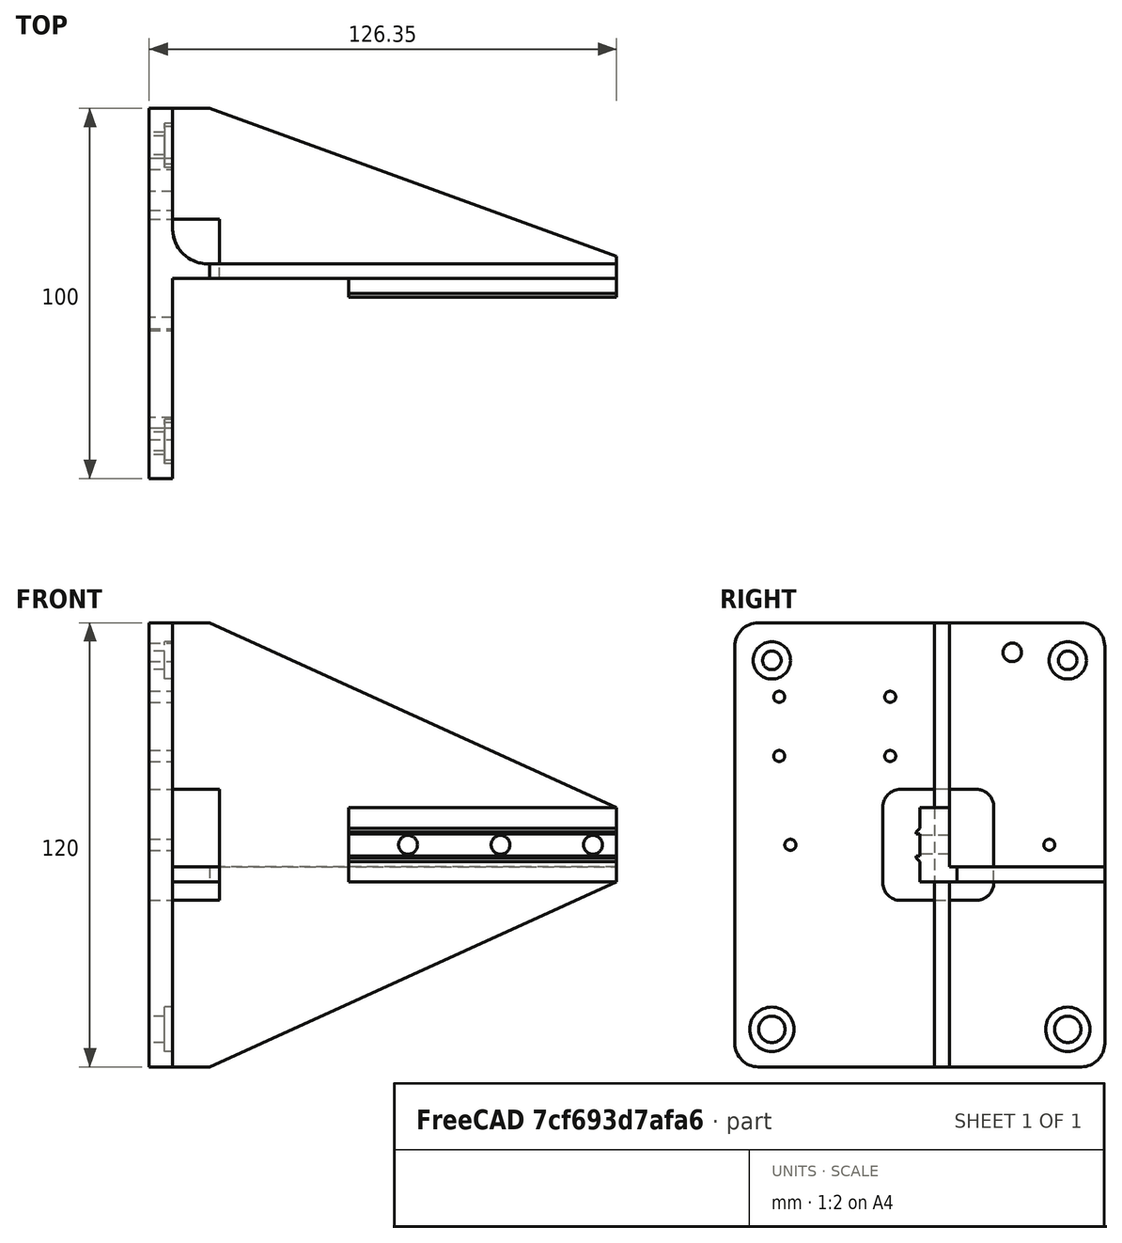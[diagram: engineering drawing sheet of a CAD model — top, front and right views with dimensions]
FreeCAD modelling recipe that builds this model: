
FCSTD DOCUMENT  (FreeCAD 0.19R23578 (Git))
Label: y_axis_carriage_block
License: All rights reserved
LicenseURL: http://en.wikipedia.org/wiki/All_rights_reserved
objects: TechDraw::DrawViewDimension×41, PartDesign::CoordinateSystem×15, Sketcher::SketchObject×10, PartDesign::Pocket×6, TechDraw::DrawProjGroupItem×3, TechDraw::DrawViewDimExtent×3, PartDesign::Pad×2, PartDesign::Fillet×2, PartDesign::Hole×2, TechDraw::DrawSVGTemplate×1, PartDesign::Body×1, TechDraw::DrawViewAnnotation×1, App::Part×1, TechDraw::DrawViewPart×1, TechDraw::DrawProjGroup×1, TechDraw::DrawViewDetail×1, TechDraw::DrawLeaderLine×1, TechDraw::DrawPage×1
note: 50 computed .brp shape members not serialized (recipe doc carries the construction recipe); baked Part::Feature solids carry a one-line shape summary decoded from their .brp

FEATURE [Sketcher::SketchObject] Sketch037
  MapMode = 5
  Support = -> [XY_Plane046]
  sketch-geometry (4):
    g0: LineSegment StartX=0 StartY=50 StartZ=0 EndX=6.35 EndY=50 EndZ=0
    g1: LineSegment StartX=6.35 StartY=50 StartZ=0 EndX=6.35 EndY=-50 EndZ=0
    g2: LineSegment StartX=6.35 StartY=-50 StartZ=0 EndX=0 EndY=-50 EndZ=0
    g3: LineSegment StartX=0 StartY=-50 StartZ=0 EndX=0 EndY=50 EndZ=0
  constraints (11):
    c: Coincident(g0,g1)
    c: Coincident(g1,g2)
    c: Coincident(g2,g3)
    c: Coincident(g3,g0)
    c: Horizontal(g0)
    c: Horizontal(g2)
    c: Vertical(g1)
    c: PointOnObject(g0,g-2)
    c: Symmetric(g2,g0,g-1)
    c: DistanceY(g2,g0) = 100
    c: DistanceX(g0,g0) = 6.35
FEATURE [PartDesign::Pad] Pad016
  AllowMultiFace = false
  Direction = (1,1,1)
  Length = 120
  Length2 = 100
  Midplane = true
  Profile = -> Sketch037
  Type = 0
FEATURE [Sketcher::SketchObject] Sketch038
  AttachmentOffset = pos=(0,0,6.35) rot=(0,0,1;0rad)
  MapMode = 5
  Placement = pos=(6.35,-1.4e-15,1.4e-15) rot=(0.57735,0.57735,0.57735;2.0944rad)
  Support = -> [YZ_Plane046]
  sketch-geometry (20):
    g0: LineSegment StartX=4 StartY=60 StartZ=0 EndX=4 EndY=10 EndZ=0
    g1: LineSegment StartX=4 StartY=10 StartZ=0 EndX=0 EndY=10 EndZ=0
    g2: LineSegment StartX=0 StartY=10 StartZ=0 EndX=0 EndY=4.5 EndZ=0
    g3: LineSegment StartX=0 StartY=4.5 StartZ=0 EndX=-1 EndY=3.5 EndZ=0
    g4: LineSegment StartX=-1 StartY=3.5 StartZ=0 EndX=-1 EndY=3 EndZ=0
    g5: LineSegment StartX=-1 StartY=3 StartZ=0 EndX=0 EndY=3 EndZ=0
    g6: LineSegment StartX=0 StartY=3 StartZ=0 EndX=0 EndY=-3 EndZ=0
    g7: LineSegment StartX=0 StartY=-3 StartZ=0 EndX=-1 EndY=-3 EndZ=0
    g8: LineSegment StartX=-1 StartY=-3 StartZ=0 EndX=-1 EndY=-3.5 EndZ=0
    g9: LineSegment StartX=-1 StartY=-3.5 StartZ=0 EndX=0 EndY=-4.5 EndZ=0
    g10: LineSegment StartX=0 StartY=-4.5 StartZ=0 EndX=0 EndY=-10 EndZ=0
    g11: LineSegment StartX=0 StartY=-10 StartZ=0 EndX=4 EndY=-10 EndZ=0
    g12: LineSegment StartX=4 StartY=-10 StartZ=0 EndX=4 EndY=-60 EndZ=0
    g13: LineSegment StartX=4 StartY=-60 StartZ=0 EndX=8 EndY=-60 EndZ=0
    g14: LineSegment StartX=8 StartY=-60 StartZ=0 EndX=8 EndY=-10 EndZ=0
    g15: LineSegment StartX=8 StartY=-10 StartZ=0 EndX=50 EndY=-10 EndZ=0
    g16: LineSegment StartX=50 StartY=-10 StartZ=0 EndX=50 EndY=-6 EndZ=0
    g17: LineSegment StartX=50 StartY=-6 StartZ=0 EndX=8 EndY=-6 EndZ=0
    g18: LineSegment StartX=8 StartY=-6 StartZ=0 EndX=8 EndY=60 EndZ=0
    g19: LineSegment StartX=8 StartY=60 StartZ=0 EndX=4 EndY=60 EndZ=0
  constraints (56):
    c: Vertical(g0)
    c: Coincident(g0,g1)
    c: Horizontal(g1)
    c: Coincident(g1,g2)
    c: Vertical(g2)
    c: Coincident(g2,g3)
    c: Coincident(g3,g4)
    c: Coincident(g4,g5)
    c: Horizontal(g5)
    c: Coincident(g5,g6)
    c: Coincident(g6,g7)
    c: Coincident(g7,g8)
    c: Coincident(g8,g9)
    c: Coincident(g9,g10)
    c: Vertical(g10)
    c: Coincident(g10,g11)
    c: Coincident(g11,g12)
    c: Vertical(g12)
    c: Coincident(g12,g13)
    c: Horizontal(g13)
    c: Coincident(g13,g14)
    c: Vertical(g14)
    c: Coincident(g14,g15)
    c: Horizontal(g15)
    c: Coincident(g15,g16)
    c: Coincident(g16,g17)
    c: Horizontal(g17)
    c: Coincident(g17,g18)
    c: Vertical(g18)
    c: Coincident(g18,g19)
    c: Coincident(g19,g0)
    c: Vertical(g4)
    c: Vertical(g6)
    c: Vertical(g16)
    c: Horizontal(g19)
    c: Horizontal(g7)
    c: Horizontal(g11)
    c: Vertical(g17,g14)
    c: Angle(g5,g3) = 0.785398
    c: Angle(g9,g7) = 0.785398
    c: DistanceY(g8,g8) = 0.5
    c: DistanceY(g6,g6) = 6
    c: Symmetric(g10,g1,g-1)
    c: Vertical(g9,g6)
    c: Symmetric(g7,g4,g-1)
    c: PointOnObject(g-1,g6)
    c: Symmetric(g3,g8,g-1)
    c: DistanceY(g-1,g2) = 4.5
    c: DistanceX(g1,g1) = 4
    c: Symmetric(g12,g0,g-1)
    c: DistanceY(g-1,g18) = 60
    c: DistanceX(g19,g19) = 4
    c: DistanceX(g-1,g15) = 50
    c: DistanceY(g-1,g0) = 10
    c: DistanceY(g16,g16) = 4
    c: Horizontal(g14,g11)
FEATURE [PartDesign::Pad] Pad017
  AllowMultiFace = false
  BaseFeature = -> Pad016
  Direction = (1,1,1)
  Length = 120
  Length2 = 100
  Profile = -> Sketch038
  Type = 0
FEATURE [Sketcher::SketchObject] Sketch039
  MapMode = 5
  Placement = pos=(0,0,0) rot=(1,0,0;1.5708rad)
  Support = -> [XZ_Plane046]
  sketch-geometry (6):
    g0: LineSegment StartX=16.35 StartY=60 StartZ=0 EndX=126.35 EndY=10 EndZ=0
    g1: LineSegment StartX=126.35 StartY=10 StartZ=0 EndX=126.35 EndY=60 EndZ=0
    g2: LineSegment StartX=126.35 StartY=60 StartZ=0 EndX=16.35 EndY=60 EndZ=0
    g3: LineSegment StartX=16.35 StartY=-60 StartZ=0 EndX=126.35 EndY=-10 EndZ=0
    g4: LineSegment StartX=126.35 StartY=-10 StartZ=0 EndX=126.35 EndY=-60 EndZ=0
    g5: LineSegment StartX=126.35 StartY=-60 StartZ=0 EndX=16.35 EndY=-60 EndZ=0
  constraints (15):
    c: Coincident(g0,g1)
    c: Coincident(g1,g2)
    c: Coincident(g2,g0)
    c: Horizontal(g2)
    c: Coincident(g3,g4)
    c: Coincident(g4,g5)
    c: Coincident(g5,g3)
    c: Symmetric(g3,g0,g-1)
    c: Symmetric(g3,g0,g-1)
    c: Symmetric(g1,g4,g-1)
    c: Vertical(g1)
    c: DistanceY(g-1,g0) = 60
    c: DistanceX(g-1,g1) = 126.35
    c: DistanceX(g-1,g0) = 16.35
    c: DistanceY(g-1,g0) = 10
FEATURE [PartDesign::Pocket] Pocket013
  AllowMultiFace = false
  BaseFeature = -> Pad017
  Length = 5
  Length2 = 100
  Midplane = true
  Profile = -> Sketch039
  Type = 1
FEATURE [Sketcher::SketchObject] Sketch040
  MapMode = 5
  Support = -> [XY_Plane046]
  sketch-geometry (3):
    g0: LineSegment StartX=16.35 StartY=50 StartZ=0 EndX=126.35 EndY=10 EndZ=0
    g1: LineSegment StartX=126.35 StartY=50 StartZ=0 EndX=126.35 EndY=10 EndZ=0
    g2: LineSegment StartX=126.35 StartY=50 StartZ=0 EndX=16.35 EndY=50 EndZ=0
  constraints (9):
    c: Coincident(g1,g0)
    c: Vertical(g1)
    c: Coincident(g2,g1)
    c: Coincident(g2,g0)
    c: Horizontal(g2)
    c: DistanceX(g-1,g0) = 16.35
    c: DistanceY(g-1,g0) = 10
    c: DistanceY(g-1,g0) = 50
    c: DistanceX(g-1,g1) = 126.35
FEATURE [PartDesign::Pocket] Pocket014
  AllowMultiFace = false
  BaseFeature = -> Pocket013
  Length = 5
  Length2 = 100
  Midplane = true
  Profile = -> Sketch040
  Type = 1
FEATURE [PartDesign::Fillet] Fillet002
  Base = -> Pocket014 [Edge17,Edge11]
  BaseFeature = -> Pocket014
  Radius = 9.525
  SupportTransform = true
  expr: Radius = 3 / 8 * 25.4
FEATURE [Sketcher::SketchObject] Sketch041
  MapMode = 5
  Placement = pos=(0,0,0) rot=(-0.57735,0.57735,0.57735;4.18879rad)
  Support = -> [YZ_Plane046]
  expr: Constraints[12] = 3 / 8 * 25.4
  sketch-geometry (8):
    g0: LineSegment StartX=-15.2375 StartY=15 StartZ=0 EndX=5.2375 EndY=15 EndZ=0
    g1: LineSegment StartX=10 StartY=10.2375 StartZ=0 EndX=10 EndY=-10.2375 EndZ=0
    g2: LineSegment StartX=5.2375 StartY=-15 StartZ=0 EndX=-15.2375 EndY=-15 EndZ=0
    g3: LineSegment StartX=-20 StartY=-10.2375 StartZ=0 EndX=-20 EndY=10.2375 EndZ=0
    g4: ArcOfCircle CenterX=5.2375 CenterY=10.2375 CenterZ=0 NormalX=0 NormalY=0 NormalZ=1 AngleXU=0 Radius=4.7625 StartAngle=0 EndAngle=1.5708
    g5: ArcOfCircle CenterX=-15.2375 CenterY=10.2375 CenterZ=0 NormalX=0 NormalY=0 NormalZ=1 AngleXU=0 Radius=4.7625 StartAngle=1.5708 EndAngle=3.14159
    g6: ArcOfCircle CenterX=-15.2375 CenterY=-10.2375 CenterZ=0 NormalX=0 NormalY=0 NormalZ=1 AngleXU=0 Radius=4.7625 StartAngle=3.14159 EndAngle=4.71239
    g7: ArcOfCircle CenterX=5.2375 CenterY=-10.2375 CenterZ=0 NormalX=0 NormalY=0 NormalZ=1 AngleXU=0 Radius=4.7625 StartAngle=4.71239 EndAngle=6.28319
  constraints (19):
    c: Horizontal(g0)
    c: Horizontal(g2)
    c: Vertical(g1)
    c: Vertical(g3)
    c: Tangent(g0,g4) = 1.5708
    c: Tangent(g1,g4) = 1.5708
    c: Tangent(g0,g5) = 1.5708
    c: Tangent(g3,g5) = 1.5708
    c: Tangent(g3,g6) = 1.5708
    c: Tangent(g2,g6) = 1.5708
    c: Tangent(g1,g7) = 1.5708
    c: Tangent(g2,g7) = 1.5708
    c: Diameter(g4) = 9.525
    c: Equal(g6,g7)
    c: DistanceY(g-1,g0) = 15
    c: DistanceX(g-1,g1) = 10
    c: Symmetric(g0,g2,g-1)
    c: Equal(g4,g7)
    c: DistanceX(g3,g-1) = 20
FEATURE [PartDesign::Pocket] Pocket015
  AllowMultiFace = false
  BaseFeature = -> Fillet002
  Length = 19
  Length2 = 100
  Profile = -> Sketch041
  Type = 0
FEATURE [Sketcher::SketchObject] Sketch042
  AttachmentOffset = pos=(0,0,6.35) rot=(0,0,1;0rad)
  MapMode = 5
  Placement = pos=(6.35,-1.4e-15,1.4e-15) rot=(0.57735,0.57735,0.57735;2.0944rad)
  Support = -> [YZ_Plane046]
  sketch-geometry (2):
    g0: Circle CenterX=-40 CenterY=49.85 CenterZ=0 NormalX=0 NormalY=0 NormalZ=1 AngleXU=0 Radius=2.505
    g1: Circle CenterX=40 CenterY=49.85 CenterZ=0 NormalX=0 NormalY=0 NormalZ=1 AngleXU=0 Radius=2.505
  constraints (5):
    c: DistanceX(g0,g-1) = 40
    c: Equal(g0,g1)
    c: Diameter(g1) = 5.01
    c: DistanceY(g-1,g1) = 49.85
    c: Symmetric(g1,g0,g-2)
FEATURE [PartDesign::Hole] Hole004
  AllowMultiFace = false
  BaseFeature = -> Pocket015
  Depth = 25
  DepthType = 1
  Diameter = 5.02
  DrillPoint = 1
  DrillPointAngle = 118
  HoleCutCountersinkAngle = 90
  HoleCutDepth = 2.18
  HoleCutDiameter = 10.1
  HoleCutType = 1
  ModelActualThread = false
  Profile = -> Sketch042
  Tapered = false
  TaperedAngle = 90
  ThreadAngle = 0
  ThreadClass = 0
  ThreadCutOffInner = 0
  ThreadCutOffOuter = 0
  ThreadDirection = 0
  ThreadFit = 0
  ThreadPitch = 0
  ThreadSize = 0
  ThreadType = 0
  Threaded = false
FEATURE [Sketcher::SketchObject] Sketch043
  AttachmentOffset = pos=(0,0,6.35) rot=(0,0,1;0rad)
  MapMode = 5
  Placement = pos=(6.35,-1.4e-15,1.4e-15) rot=(0.57735,0.57735,0.57735;2.0944rad)
  Support = -> [YZ_Plane046]
  sketch-geometry (2):
    g0: Circle CenterX=-40 CenterY=-49.85 CenterZ=0 NormalX=0 NormalY=0 NormalZ=1 AngleXU=0 Radius=3.57
    g1: Circle CenterX=40 CenterY=-49.85 CenterZ=0 NormalX=0 NormalY=0 NormalZ=1 AngleXU=0 Radius=3.57
  constraints (5):
    c: DistanceX(g0,g-1) = 40
    c: Equal(g0,g1)
    c: Diameter(g1) = 7.14
    c: Symmetric(g1,g0,g-2)
    c: DistanceY(g0,g-1) = 49.85
FEATURE [PartDesign::Hole] Hole005
  AllowMultiFace = false
  BaseFeature = -> Hole004
  Depth = 25
  DepthType = 1
  Diameter = 7.14
  DrillPoint = 1
  DrillPointAngle = 118
  HoleCutCountersinkAngle = 90
  HoleCutDepth = 2.18
  HoleCutDiameter = 12
  HoleCutType = 1
  ModelActualThread = false
  Profile = -> Sketch043
  Tapered = false
  TaperedAngle = 90
  ThreadAngle = 0
  ThreadClass = 0
  ThreadCutOffInner = 0
  ThreadCutOffOuter = 0
  ThreadDirection = 0
  ThreadFit = 0
  ThreadPitch = 0
  ThreadSize = 0
  ThreadType = 0
  Threaded = false
FEATURE [TechDraw::DrawSVGTemplate] Template008
  EditableTexts = Author=Alex Neufeld; DWG_num=2020-111; Date=25/05/2020; Revision=1; Scale=1:2; Subtitle=Machined from billet; Title=Carriage Block
  Height = 215.9
  Orientation = 1
  Width = 279.4
FEATURE [Sketcher::SketchObject] Sketch082
  AttachmentOffset = pos=(0,0,6.35) rot=(0,0,1;0rad)
  MapMode = 5
  Placement = pos=(6.35,-1.4e-15,1.4e-15) rot=(0.57735,0.57735,0.57735;2.0944rad)
  Support = -> [YZ_Plane046]
  sketch-geometry (7):
    g0: Circle CenterX=-38 CenterY=40 CenterZ=0 NormalX=0 NormalY=0 NormalZ=1 AngleXU=0 Radius=1.5
    g1: Circle CenterX=-38 CenterY=24 CenterZ=0 NormalX=0 NormalY=0 NormalZ=1 AngleXU=0 Radius=1.5
    g2: Circle CenterX=-8 CenterY=40 CenterZ=0 NormalX=0 NormalY=0 NormalZ=1 AngleXU=0 Radius=1.5
    g3: Circle CenterX=-8 CenterY=24 CenterZ=0 NormalX=0 NormalY=0 NormalZ=1 AngleXU=0 Radius=1.5
    g4: Circle CenterX=35 CenterY=0 CenterZ=0 NormalX=0 NormalY=0 NormalZ=1 AngleXU=0 Radius=1.5
    g5: Circle CenterX=25 CenterY=52 CenterZ=0 NormalX=0 NormalY=0 NormalZ=1 AngleXU=0 Radius=2.5
    g6: Circle CenterX=-35 CenterY=0 CenterZ=0 NormalX=0 NormalY=0 NormalZ=1 AngleXU=0 Radius=1.5
  constraints (21):
    c: Vertical(g2,g3)
    c: Vertical(g0,g1)
    c: Horizontal(g0,g2)
    c: Horizontal(g1,g3)
    c: Equal(g0,g1)
    c: Equal(g1,g3)
    c: Equal(g3,g2)
    c: Diameter(g2) = 3
    c: DistanceX(g3,g-1) = 8
    c: DistanceY(g-1,g3) = 24
    c: DistanceY(g3,g2) = 16
    c: DistanceX(g1,g3) = 30
    c: PointOnObject(g4,g-1)
    c: Diameter(g4) = 3
    c: DistanceX(g-1,g4) = 35
    c: Diameter(g5) = 5
    c: DistanceY(g-1,g5) = 52
    c: DistanceX(g-1,g5) = 25
    c: PointOnObject(g6,g-1)
    c: Equal(g6,g4)
    c: DistanceX(g6,g-1) = 35
FEATURE [PartDesign::Pocket] Pocket022
  BaseFeature = -> Hole005
  Length = 5
  Length2 = 100
  Profile = -> Sketch082
  Type = 1
FEATURE [Sketcher::SketchObject] Sketch083
  MapMode = 5
  Placement = pos=(0,0,0) rot=(1,0,0;1.5708rad)
  Support = -> [XZ_Plane046]
  sketch-geometry (3):
    g0: Circle CenterX=70 CenterY=0 CenterZ=0 NormalX=0 NormalY=0 NormalZ=1 AngleXU=0 Radius=2.55
    g1: Circle CenterX=120 CenterY=0 CenterZ=0 NormalX=0 NormalY=0 NormalZ=1 AngleXU=0 Radius=2.55
    g2: Circle CenterX=95 CenterY=0 CenterZ=0 NormalX=0 NormalY=0 NormalZ=1 AngleXU=0 Radius=2.55
  constraints (9):
    c: PointOnObject(g0,g-1)
    c: PointOnObject(g1,g-1)
    c: PointOnObject(g2,g-1)
    c: Equal(g0,g2)
    c: Equal(g2,g1)
    c: Diameter(g1) = 5.1
    c: DistanceX(g2,g1) = 25
    c: DistanceX(g0,g2) = 25
    c: DistanceX(g-1,g0) = 70
FEATURE [PartDesign::Pocket] Pocket023
  BaseFeature = -> Pocket022
  Length = 5
  Length2 = 100
  Profile = -> Sketch083
  Type = 1
FEATURE [PartDesign::Fillet] Fillet007
  Base = -> Pocket023 [Edge82,Edge17,Edge24,Edge13]
  BaseFeature = -> Pocket023
  Radius = 6.35
  SupportTransform = true
FEATURE [Sketcher::SketchObject] Sketch084
  MapMode = 5
  Support = -> [XY_Plane046]
  sketch-geometry (4):
    g0: LineSegment StartX=10 StartY=4 StartZ=0 EndX=54 EndY=4 EndZ=0
    g1: LineSegment StartX=54 StartY=4 StartZ=0 EndX=54 EndY=-21 EndZ=0
    g2: LineSegment StartX=54 StartY=-21 StartZ=0 EndX=10 EndY=-21 EndZ=0
    g3: LineSegment StartX=10 StartY=-21 StartZ=0 EndX=10 EndY=4 EndZ=0
  constraints (12):
    c: Coincident(g0,g1)
    c: Coincident(g1,g2)
    c: Coincident(g2,g3)
    c: Coincident(g3,g0)
    c: Horizontal(g0)
    c: Horizontal(g2)
    c: Vertical(g1)
    c: Vertical(g3)
    c: DistanceX(g-1,g0) = 10
    c: DistanceX(g2,g2) = 44
    c: DistanceY(g3,g3) = 25
    c: DistanceY(g-1,g0) = 4
FEATURE [PartDesign::Pocket] Pocket024
  BaseFeature = -> Fillet007
  Length = 20
  Length2 = 100
  Midplane = true
  Profile = -> Sketch084
  Type = 0
FEATURE [PartDesign::Body] Body016  label="Body"
  Group = -> [Sketch037,Pad016,Sketch038,Pad017,Sketch039,Pocket013,Sketch040,Pocket014,Fillet002,Sketch041,Pocket015,Sketch042,Hole004,Sketch043,Hole005,Sketch082,Pocket022,Sketch083,Pocket023,Fillet007,Sketch084,Pocket024]
  Origin = -> Origin046
  Tip = -> Pocket024
FEATURE [TechDraw::DrawViewAnnotation] Annotation009
  Font = Sans Serif
  LineSpace = 80
  LockPosition = false
  MaxWidth = -1
  Rotation = 0
  ScaleType = 0
  Text = Counterbore depth 2.18mm
  TextSize = 2.5
  TextStyle = 0
  X = 41.3094
  Y = 48.5238
FEATURE [PartDesign::CoordinateSystem] LCS_1
  AttacherType = Attacher::AttachEngine3D
  MapMode = 11
  Placement = pos=(70,8,1.8e-15) rot=(0.57735,-0.57735,0.57735;2.0944rad)
  Support = -> [Fillet007]
FEATURE [PartDesign::CoordinateSystem] LCS_2
  AttacherType = Attacher::AttachEngine3D
  MapMode = 11
  Placement = pos=(95,8,1.8e-15) rot=(0.57735,-0.57735,0.57735;2.0944rad)
  Support = -> [Fillet007]
FEATURE [PartDesign::CoordinateSystem] LCS_3
  AttacherType = Attacher::AttachEngine3D
  MapMode = 11
  Placement = pos=(120,8,1.8e-15) rot=(0.57735,-0.57735,0.57735;2.0944rad)
  Support = -> [Fillet007]
FEATURE [PartDesign::CoordinateSystem] LCS_4
  AttacherType = Attacher::AttachEngine3D
  AttachmentOffset = pos=(0,-15,0) rot=(0,0,1;0rad)
  MapMode = 45
  Placement = pos=(57.675,-1.1e-14,1.91e-14) rot=(0.57735,0.57735,0.57735;4.18879rad)
  Support = -> [Fillet007]
FEATURE [PartDesign::CoordinateSystem] LCS_5
  AttacherType = Attacher::AttachEngine3D
  MapMode = 11
  Placement = pos=(6.35,-38,40) rot=(0.707107,0,0.707107;3.14159rad)
  Support = -> [Fillet007]
FEATURE [PartDesign::CoordinateSystem] LCS_6
  AttacherType = Attacher::AttachEngine3D
  MapMode = 11
  Placement = pos=(6.35,-8,40) rot=(0.707107,0,0.707107;3.14159rad)
  Support = -> [Fillet007]
FEATURE [PartDesign::CoordinateSystem] LCS_7
  AttacherType = Attacher::AttachEngine3D
  MapMode = 11
  Placement = pos=(6.35,-38,24) rot=(0.707107,0,0.707107;3.14159rad)
  Support = -> [Fillet007]
FEATURE [PartDesign::CoordinateSystem] LCS_8
  AttacherType = Attacher::AttachEngine3D
  MapMode = 11
  Placement = pos=(6.35,-8,24) rot=(0.707107,0,0.707107;3.14159rad)
  Support = -> [Fillet007]
FEATURE [PartDesign::CoordinateSystem] LCS_9
  AttacherType = Attacher::AttachEngine3D
  MapMode = 11
  Placement = pos=(4.17,-40,49.85) rot=(0.57735,0.57735,0.57735;2.0944rad)
  Support = -> [Fillet007]
FEATURE [PartDesign::CoordinateSystem] LCS_10
  AttacherType = Attacher::AttachEngine3D
  MapMode = 11
  Placement = pos=(4.17,40,49.85) rot=(0.57735,0.57735,0.57735;2.0944rad)
  Support = -> [Fillet007]
FEATURE [PartDesign::CoordinateSystem] LCS_11
  AttacherType = Attacher::AttachEngine3D
  MapMode = 11
  Placement = pos=(0,-40,49.85) rot=(-0.57735,0.57735,0.57735;4.18879rad)
  Support = -> [Fillet007]
FEATURE [PartDesign::CoordinateSystem] LCS_12
  AttacherType = Attacher::AttachEngine3D
  MapMode = 11
  Placement = pos=(0,40,49.85) rot=(-0.57735,0.57735,0.57735;4.18879rad)
  Support = -> [Fillet007]
FEATURE [PartDesign::CoordinateSystem] LCS_13
  AttacherType = Attacher::AttachEngine3D
  MapMode = 11
  Placement = pos=(0,40,-49.85) rot=(-0.57735,0.57735,0.57735;4.18879rad)
  Support = -> [Fillet007]
FEATURE [PartDesign::CoordinateSystem] LCS_14
  AttacherType = Attacher::AttachEngine3D
  MapMode = 11
  Placement = pos=(0,-40,-49.85) rot=(-0.57735,0.57735,0.57735;4.18879rad)
  Support = -> [Fillet007]
FEATURE [PartDesign::CoordinateSystem] LCS_15
  AttacherType = Attacher::AttachEngine3D
  AttachmentOffset = pos=(6,0,0) rot=(0,0,1;0rad)
  MapMode = 45
  Placement = pos=(6.35,-23,38) rot=(0.707107,0,0.707107;3.14159rad)
  Support = -> [Fillet007]
FEATURE [App::Part] Part026  label="y_axis_carriage_block"
  Group = -> [Body016,LCS_1,LCS_2,LCS_3,LCS_4,LCS_5,LCS_6,LCS_7,LCS_8,LCS_9,LCS_10,LCS_11,LCS_12,LCS_13,LCS_14,LCS_15]
  Origin = -> Origin040
FEATURE [TechDraw::DrawViewPart] View009
  CoarseView = false
  Direction = (0.577,-0.577,0.577)
  Focus = 100
  HardHidden = false
  IsoCount = 0
  IsoHidden = false
  IsoVisible = false
  LockPosition = false
  Perspective = false
  Rotation = 0
  Scale = 0.33
  ScaleType = 0
  SeamHidden = false
  SeamVisible = true
  SmoothHidden = false
  SmoothVisible = true
  Source = -> [Part026]
  X = 34.7513
  XDirection = (0.707,0.707,0)
  Y = 180.756
FEATURE [TechDraw::DrawProjGroupItem] ProjItem029  label="Front008"
  CoarseView = false
  Direction = (0,-1,0)
  Focus = 100
  HardHidden = false
  IsoCount = 0
  IsoHidden = false
  IsoVisible = false
  LockPosition = true
  Perspective = false
  Rotation = 0
  RotationVector = (1,0,0)
  Scale = 0.5
  ScaleType = 2
  SeamHidden = false
  SeamVisible = true
  SmoothHidden = false
  SmoothVisible = true
  Source = -> [Part026]
  Type = 0
  X = 0
  XDirection = (1,0,0)
  Y = 0
FEATURE [TechDraw::DrawProjGroupItem] ProjItem030  label="Bottom006"
  CoarseView = false
  Direction = (0,0,-1)
  Focus = 100
  HardHidden = false
  IsoCount = 0
  IsoHidden = false
  IsoVisible = false
  LockPosition = true
  Perspective = false
  Rotation = 0
  RotationVector = (1,0,0)
  ScaleType = 2
  SeamHidden = false
  SeamVisible = true
  SmoothHidden = false
  SmoothVisible = true
  Source = -> [Part026]
  Type = 5
  X = 0
  XDirection = (1,0,0)
  Y = 75
FEATURE [TechDraw::DrawProjGroupItem] ProjItem031  label="Right004"
  CoarseView = false
  Direction = (1,-1e-16,0)
  Focus = 100
  HardHidden = false
  IsoCount = 0
  IsoHidden = false
  IsoVisible = false
  LockPosition = true
  Perspective = false
  Rotation = 0
  RotationVector = (1,0,0)
  ScaleType = 2
  SeamHidden = false
  SeamVisible = true
  SmoothHidden = false
  SmoothVisible = true
  Source = -> [Part026]
  Type = 2
  X = -78.175
  XDirection = (1e-16,1,0)
  Y = 0
FEATURE [TechDraw::DrawProjGroup] ProjGroup008
  Anchor = -> ProjItem029
  AutoDistribute = true
  LockPosition = true
  ProjectionType = 0
  Rotation = 0
  Scale = 0.5
  ScaleType = 2
  Source = -> [Part026]
  Views = -> [ProjItem029,ProjItem030,ProjItem031]
  X = 151.564
  Y = 83.8481
  spacingX = 15
  spacingY = 15
FEATURE [TechDraw::DrawViewDimExtent] DimExtent005
  Arbitrary = false
  ArbitraryTolerances = false
  CosmeticTags = 0b52134a-8e6d-49b5-af52-e823de50e186 | 81887f05-93b7-4f57-9f60-22745010a6d3
  DirExtent = 0
  FormatSpec = %.2f
  FormatSpecOverTolerance = %+.2f
  FormatSpecUnderTolerance = %+.2f
  Inverted = false
  LockPosition = false
  MeasureType = 1
  OverTolerance = 0
  References2D = -> [ProjItem031]
  Rotation = 0
  ScaleType = 0
  Source = -> [ProjItem031]
  TheoreticalExact = false
  Type = 1
  UnderTolerance = 0
  X = 0.546024
  Y = -36.8813
FEATURE [TechDraw::DrawViewDimExtent] DimExtent006
  Arbitrary = false
  ArbitraryTolerances = false
  CosmeticTags = 3ffed1fc-5ad0-4ec7-b127-2a2c0d19fe92 | 0dd20677-cea0-4880-986b-66a6b66657e0
  DirExtent = 1
  FormatSpec = %.2f
  FormatSpecOverTolerance = %+.2f
  FormatSpecUnderTolerance = %+.2f
  Inverted = false
  LockPosition = false
  MeasureType = 1
  OverTolerance = 0
  References2D = -> [ProjItem031]
  Rotation = 0
  ScaleType = 0
  Source = -> [ProjItem031]
  TheoreticalExact = false
  Type = 2
  UnderTolerance = 0
  X = -38.9861
  Y = 1.54868
FEATURE [TechDraw::DrawViewDimExtent] DimExtent007
  Arbitrary = false
  ArbitraryTolerances = false
  CosmeticTags = cf14e2b6-0178-4381-bba3-44740000f48a | 09ec5796-2379-4229-aecd-7de02c0fdcc3
  DirExtent = 0
  FormatSpec = %.2f
  FormatSpecOverTolerance = %+.2f
  FormatSpecUnderTolerance = %+.2f
  Inverted = false
  LockPosition = false
  MeasureType = 1
  OverTolerance = 0
  References2D = -> [ProjItem029]
  Rotation = 0
  ScaleType = 0
  Source = -> [ProjItem029]
  TheoreticalExact = false
  Type = 1
  UnderTolerance = 0
  X = -2.12632
  Y = -52.8642
FEATURE [TechDraw::DrawViewDetail] Detail
  AnchorPoint = (0.6,0.3,0)
  BaseView = -> ProjItem031
  CoarseView = false
  Direction = (1,-1e-16,0)
  Focus = 100
  HardHidden = false
  IsoCount = 0
  IsoHidden = false
  IsoVisible = false
  LockPosition = false
  Perspective = false
  Radius = 15
  Reference = 1
  Rotation = 0
  ScaleType = 0
  SeamHidden = false
  SeamVisible = true
  SmoothHidden = false
  SmoothVisible = true
  Source = -> [Part026]
  X = 239.468
  XDirection = (1e-16,1,0)
  Y = 166.543
FEATURE [TechDraw::DrawViewDimension] Dimension122
  Arbitrary = false
  ArbitraryTolerances = false
  FormatSpec = %.2f
  FormatSpecOverTolerance = %+.2f
  FormatSpecUnderTolerance = %+.2f
  Inverted = false
  LockPosition = false
  MeasureType = 1
  OverTolerance = 0
  References2D = -> [ProjItem031]
  Rotation = 0
  ScaleType = 0
  TheoreticalExact = false
  Type = 1
  UnderTolerance = 0
  X = -35.1344
  Y = 43.6728
FEATURE [TechDraw::DrawViewDimension] Dimension123
  Arbitrary = false
  ArbitraryTolerances = false
  FormatSpec = %.2f
  FormatSpecOverTolerance = %+.2f
  FormatSpecUnderTolerance = %+.2f
  Inverted = false
  LockPosition = false
  MeasureType = 1
  OverTolerance = 0
  References2D = -> [ProjItem031]
  Rotation = 0
  ScaleType = 0
  TheoreticalExact = false
  Type = 1
  UnderTolerance = 0
  X = -1.81485
  Y = 52.077
FEATURE [TechDraw::DrawViewDimension] Dimension124
  Arbitrary = false
  ArbitraryTolerances = false
  FormatSpec = %.2f
  FormatSpecOverTolerance = %+.2f
  FormatSpecUnderTolerance = %+.2f
  Inverted = false
  LockPosition = false
  MeasureType = 1
  OverTolerance = 0
  References2D = -> [ProjItem031]
  Rotation = 0
  ScaleType = 0
  TheoreticalExact = false
  Type = 1
  UnderTolerance = 0
  X = -5.76535
  Y = 36.2849
FEATURE [TechDraw::DrawViewDimension] Dimension125
  Arbitrary = false
  ArbitraryTolerances = false
  FormatSpec = %.2f
  FormatSpecOverTolerance = %+.2f
  FormatSpecUnderTolerance = %+.2f
  Inverted = false
  LockPosition = false
  MeasureType = 1
  OverTolerance = 0
  References2D = -> [ProjItem031]
  Rotation = 0
  ScaleType = 0
  TheoreticalExact = false
  Type = 1
  UnderTolerance = 0
  X = -22
  Y = 17.732
FEATURE [TechDraw::DrawViewDimension] Dimension126
  Arbitrary = false
  ArbitraryTolerances = false
  FormatSpec = %.2f
  FormatSpecOverTolerance = %+.2f
  FormatSpecUnderTolerance = %+.2f
  Inverted = false
  LockPosition = false
  MeasureType = 1
  OverTolerance = 0
  References2D = -> [ProjItem031]
  Rotation = 0
  ScaleType = 0
  TheoreticalExact = false
  Type = 1
  UnderTolerance = 0
  X = -10.718
  Y = 24.2808
FEATURE [TechDraw::DrawViewDimension] Dimension127
  Arbitrary = false
  ArbitraryTolerances = false
  FormatSpec = %.2f
  FormatSpecOverTolerance = %+.2f
  FormatSpecUnderTolerance = %+.2f
  Inverted = false
  LockPosition = false
  MeasureType = 1
  OverTolerance = 0
  References2D = -> [ProjItem031]
  Rotation = 0
  ScaleType = 0
  TheoreticalExact = false
  Type = 1
  UnderTolerance = 0
  X = -11.5378
  Y = -9.88744
FEATURE [TechDraw::DrawViewDimension] Dimension128
  Arbitrary = false
  ArbitraryTolerances = false
  FormatSpec = %.2f
  FormatSpecOverTolerance = %+.2f
  FormatSpecUnderTolerance = %+.2f
  Inverted = false
  LockPosition = false
  MeasureType = 1
  OverTolerance = 0
  References2D = -> [ProjItem031]
  Rotation = 0
  ScaleType = 0
  TheoreticalExact = false
  Type = 1
  UnderTolerance = 0
  X = -12.013
  Y = 5.78028
FEATURE [TechDraw::DrawViewDimension] Dimension129
  Arbitrary = false
  ArbitraryTolerances = false
  FormatSpec = %.2f
  FormatSpecOverTolerance = %+.2f
  FormatSpecUnderTolerance = %+.2f
  Inverted = false
  LockPosition = false
  MeasureType = 1
  OverTolerance = 0
  References2D = -> [ProjItem031]
  Rotation = 0
  ScaleType = 0
  TheoreticalExact = false
  Type = 2
  UnderTolerance = 0
  X = -50.7316
  Y = 30.446
FEATURE [TechDraw::DrawViewDimension] Dimension130
  Arbitrary = false
  ArbitraryTolerances = false
  FormatSpec = %.2f
  FormatSpecOverTolerance = %+.2f
  FormatSpecUnderTolerance = %+.2f
  Inverted = false
  LockPosition = false
  MeasureType = 1
  OverTolerance = 0
  References2D = -> [ProjItem031]
  Rotation = 0
  ScaleType = 0
  TheoreticalExact = false
  Type = 2
  UnderTolerance = 0
  X = 12.4007
  Y = 42.2097
FEATURE [TechDraw::DrawViewDimension] Dimension131
  Arbitrary = false
  ArbitraryTolerances = false
  FormatSpec = %.2f
  FormatSpecOverTolerance = %+.2f
  FormatSpecUnderTolerance = %+.2f
  Inverted = false
  LockPosition = false
  MeasureType = 1
  OverTolerance = 0
  References2D = -> [ProjItem031]
  Rotation = 0
  ScaleType = 0
  TheoreticalExact = false
  Type = 2
  UnderTolerance = 0
  X = -47.4173
  Y = 1.82714
FEATURE [TechDraw::DrawViewDimension] Dimension132
  Arbitrary = false
  ArbitraryTolerances = false
  FormatSpec = %.2f
  FormatSpecOverTolerance = %+.2f
  FormatSpecUnderTolerance = %+.2f
  Inverted = false
  LockPosition = false
  MeasureType = 1
  OverTolerance = 0
  References2D = -> [ProjItem029]
  Rotation = 0
  ScaleType = 0
  TheoreticalExact = false
  Type = 1
  UnderTolerance = 0
  X = -17.705
  Y = 21.9071
FEATURE [TechDraw::DrawViewDimension] Dimension133
  Arbitrary = false
  ArbitraryTolerances = false
  FormatSpec = %.2f
  FormatSpecOverTolerance = %+.2f
  FormatSpecUnderTolerance = %+.2f
  Inverted = false
  LockPosition = false
  MeasureType = 1
  OverTolerance = 0
  References2D = -> [ProjItem029]
  Rotation = 0
  ScaleType = 0
  TheoreticalExact = false
  Type = 1
  UnderTolerance = 0
  X = -5.86702
  Y = 36.381
FEATURE [TechDraw::DrawViewDimension] Dimension134
  Arbitrary = false
  ArbitraryTolerances = false
  FormatSpec = %.2f
  FormatSpecOverTolerance = %+.2f
  FormatSpecUnderTolerance = %+.2f
  Inverted = false
  LockPosition = false
  MeasureType = 1
  OverTolerance = 0
  References2D = -> [ProjItem029]
  Rotation = 0
  ScaleType = 0
  TheoreticalExact = false
  Type = 1
  UnderTolerance = 0
  X = -13.2974
  Y = -12.9991
FEATURE [TechDraw::DrawViewDimension] Dimension135
  Arbitrary = false
  ArbitraryTolerances = false
  FormatSpec = %.2f
  FormatSpecOverTolerance = %+.2f
  FormatSpecUnderTolerance = %+.2f
  Inverted = false
  LockPosition = false
  MeasureType = 1
  OverTolerance = 0
  References2D = -> [ProjItem029]
  Rotation = 0
  ScaleType = 0
  TheoreticalExact = false
  Type = 1
  UnderTolerance = 0
  X = -17.2834
  Y = -20.9932
FEATURE [TechDraw::DrawViewDimension] Dimension137
  Arbitrary = false
  ArbitraryTolerances = false
  FormatSpec = %.2f
  FormatSpecOverTolerance = %+.2f
  FormatSpecUnderTolerance = %+.2f
  Inverted = false
  LockPosition = false
  MeasureType = 1
  OverTolerance = 0
  References2D = -> [ProjItem029]
  Rotation = 0
  ScaleType = 0
  TheoreticalExact = false
  Type = 2
  UnderTolerance = 0
  X = -6.65506
  Y = 19.3725
FEATURE [TechDraw::DrawViewDimension] Dimension138
  Arbitrary = false
  ArbitraryTolerances = false
  FormatSpec = %.2f
  FormatSpecOverTolerance = %+.2f
  FormatSpecUnderTolerance = %+.2f
  Inverted = false
  LockPosition = false
  MeasureType = 1
  OverTolerance = 0
  References2D = -> [ProjItem029]
  Rotation = 0
  ScaleType = 0
  TheoreticalExact = false
  Type = 2
  UnderTolerance = 0
  X = -41.3114
  Y = 6.58101
FEATURE [TechDraw::DrawViewDimension] Dimension139
  Arbitrary = false
  ArbitraryTolerances = false
  FormatSpec = %.2f
  FormatSpecOverTolerance = %+.2f
  FormatSpecUnderTolerance = %+.2f
  Inverted = false
  LockPosition = false
  MeasureType = 1
  OverTolerance = 0
  References2D = -> [ProjItem031]
  Rotation = 0
  ScaleType = 0
  TheoreticalExact = false
  Type = 2
  UnderTolerance = 0
  X = -32.0512
  Y = 1.80996
FEATURE [TechDraw::DrawViewDimension] Dimension140
  Arbitrary = false
  ArbitraryTolerances = false
  FormatSpec = %.2f
  FormatSpecOverTolerance = %+.2f
  FormatSpecUnderTolerance = %+.2f
  Inverted = false
  LockPosition = false
  MeasureType = 1
  OverTolerance = 0
  References2D = -> [Detail]
  Rotation = 0
  ScaleType = 0
  TheoreticalExact = false
  Type = 2
  UnderTolerance = 0
  X = -21.7884
  Y = -0.002626
FEATURE [TechDraw::DrawViewDimension] Dimension141
  Arbitrary = false
  ArbitraryTolerances = false
  FormatSpec = %.2f
  FormatSpecOverTolerance = %+.2f
  FormatSpecUnderTolerance = %+.2f
  Inverted = false
  LockPosition = false
  MeasureType = 1
  OverTolerance = 0
  References2D = -> [Detail]
  Rotation = 0
  ScaleType = 0
  TheoreticalExact = false
  Type = 1
  UnderTolerance = 0
  X = -21.7021
  Y = 21.1806
FEATURE [TechDraw::DrawViewDimension] Dimension142
  Arbitrary = false
  ArbitraryTolerances = false
  FormatSpec = %.2f
  FormatSpecOverTolerance = %+.2f
  FormatSpecUnderTolerance = %+.2f
  Inverted = false
  LockPosition = false
  MeasureType = 1
  OverTolerance = 0
  References2D = -> [Detail]
  Rotation = 0
  ScaleType = 0
  TheoreticalExact = false
  Type = 2
  UnderTolerance = 0
  X = 20.1901
  Y = 0.000218
FEATURE [TechDraw::DrawViewDimension] Dimension143
  Arbitrary = false
  ArbitraryTolerances = false
  FormatSpec = %.2f
  FormatSpecOverTolerance = %+.2f
  FormatSpecUnderTolerance = %+.2f
  Inverted = false
  LockPosition = false
  MeasureType = 1
  OverTolerance = 0
  References2D = -> [ProjItem029]
  Rotation = 0
  ScaleType = 0
  TheoreticalExact = false
  Type = 2
  UnderTolerance = 0
  X = 47.1537
  Y = 13.8966
FEATURE [TechDraw::DrawViewDimension] Dimension144
  Arbitrary = false
  ArbitraryTolerances = false
  FormatSpec = %.2f
  FormatSpecOverTolerance = %+.2f
  FormatSpecUnderTolerance = %+.2f
  Inverted = false
  LockPosition = false
  MeasureType = 1
  OverTolerance = 0
  References2D = -> [ProjItem029]
  Rotation = 0
  ScaleType = 0
  TheoreticalExact = false
  Type = 1
  UnderTolerance = 0
  X = -14.2172
  Y = -32.7571
FEATURE [TechDraw::DrawViewDimension] Dimension145
  Arbitrary = false
  ArbitraryTolerances = false
  FormatSpec = %.2f
  FormatSpecOverTolerance = %+.2f
  FormatSpecUnderTolerance = %+.2f
  Inverted = false
  LockPosition = false
  MeasureType = 1
  OverTolerance = 0
  References2D = -> [ProjItem029]
  Rotation = 0
  ScaleType = 0
  TheoreticalExact = false
  Type = 1
  UnderTolerance = 0
  X = -6.15148
  Y = -38.2043
FEATURE [TechDraw::DrawViewDimension] Dimension146
  Arbitrary = false
  ArbitraryTolerances = false
  FormatSpec = %.2f
  FormatSpecOverTolerance = %+.2f
  FormatSpecUnderTolerance = %+.2f
  Inverted = false
  LockPosition = false
  MeasureType = 1
  OverTolerance = 0
  References2D = -> [ProjItem029]
  Rotation = 0
  ScaleType = 0
  TheoreticalExact = false
  Type = 1
  UnderTolerance = 0
  X = 1.21389
  Y = -44.8965
FEATURE [TechDraw::DrawViewDimension] Dimension147
  Arbitrary = false
  ArbitraryTolerances = false
  FormatSpec = %.2f
  FormatSpecOverTolerance = %+.2f
  FormatSpecUnderTolerance = %+.2f
  Inverted = false
  LockPosition = false
  MeasureType = 1
  OverTolerance = 0
  References2D = -> [ProjItem030]
  Rotation = 0
  ScaleType = 0
  TheoreticalExact = false
  Type = 1
  UnderTolerance = 0
  X = -5.8931
  Y = -28.1572
FEATURE [TechDraw::DrawViewDimension] Dimension151
  Arbitrary = false
  ArbitraryTolerances = false
  FormatSpec = %.2f
  FormatSpecOverTolerance = %+.2f
  FormatSpecUnderTolerance = %+.2f
  Inverted = false
  LockPosition = false
  MeasureType = 1
  OverTolerance = 0
  References2D = -> [ProjItem031]
  Rotation = 0
  ScaleType = 0
  TheoreticalExact = false
  Type = 2
  UnderTolerance = 0
  X = 20.9262
  Y = 15.2759
FEATURE [TechDraw::DrawViewDimension] Dimension152
  Arbitrary = false
  ArbitraryTolerances = false
  FormatSpec = %.2f
  FormatSpecOverTolerance = %+.2f
  FormatSpecUnderTolerance = %+.2f
  Inverted = false
  LockPosition = false
  MeasureType = 1
  OverTolerance = 0
  References2D = -> [ProjItem031]
  Rotation = 0
  ScaleType = 0
  TheoreticalExact = false
  Type = 2
  UnderTolerance = 0
  X = 28.2581
  Y = 12.2954
FEATURE [TechDraw::DrawViewDimension] Dimension153
  Arbitrary = false
  ArbitraryTolerances = false
  FormatSpec = %.2f
  FormatSpecOverTolerance = %+.2f
  FormatSpecUnderTolerance = %+.2f
  Inverted = false
  LockPosition = false
  MeasureType = 1
  OverTolerance = 0
  References2D = -> [ProjItem030]
  Rotation = 0
  ScaleType = 0
  TheoreticalExact = false
  Type = 2
  UnderTolerance = 0
  X = 30.8298
  Y = 12.7841
FEATURE [TechDraw::DrawViewDimension] Dimension154
  Arbitrary = false
  ArbitraryTolerances = false
  FormatSpec = %.2f
  FormatSpecOverTolerance = %+.2f
  FormatSpecUnderTolerance = %+.2f
  Inverted = false
  LockPosition = false
  MeasureType = 1
  OverTolerance = 0
  References2D = -> [ProjItem030]
  Rotation = 0
  ScaleType = 0
  TheoreticalExact = false
  Type = 2
  UnderTolerance = 0
  X = 36.2533
  Y = 10.6476
FEATURE [TechDraw::DrawViewDimension] Dimension155
  Arbitrary = false
  ArbitraryTolerances = false
  FormatSpec = %.2f
  FormatSpecOverTolerance = %+.2f
  FormatSpecUnderTolerance = %+.2f
  Inverted = false
  LockPosition = false
  MeasureType = 1
  OverTolerance = 0
  References2D = -> [ProjItem030]
  Rotation = 0
  ScaleType = 0
  TheoreticalExact = false
  Type = 2
  UnderTolerance = 0
  X = 41.3679
  Y = 8.79513
FEATURE [TechDraw::DrawViewDimension] Dimension156
  Arbitrary = false
  ArbitraryTolerances = false
  FormatSpec = %.2f
  FormatSpecOverTolerance = %+.2f
  FormatSpecUnderTolerance = %+.2f
  Inverted = false
  LockPosition = false
  MeasureType = 1
  OverTolerance = 0
  References2D = -> [ProjItem030]
  Rotation = 0
  ScaleType = 0
  TheoreticalExact = false
  Type = 2
  UnderTolerance = 0
  X = 46.9087
  Y = 7.44269
FEATURE [TechDraw::DrawViewDimension] Dimension157
  Arbitrary = false
  ArbitraryTolerances = false
  FormatSpec = %.2f
  FormatSpecOverTolerance = %+.2f
  FormatSpecUnderTolerance = %+.2f
  Inverted = false
  LockPosition = false
  MeasureType = 1
  OverTolerance = 0
  References2D = -> [ProjItem031]
  Rotation = 0
  ScaleType = 0
  TheoreticalExact = false
  Type = 1
  UnderTolerance = 0
  X = -15
  Y = -15.9719
FEATURE [TechDraw::DrawViewDimension] Dimension158
  Arbitrary = false
  ArbitraryTolerances = false
  FormatSpec = %.2f
  FormatSpecOverTolerance = %+.2f
  FormatSpecUnderTolerance = %+.2f
  Inverted = false
  LockPosition = false
  MeasureType = 1
  OverTolerance = 0
  References2D = -> [ProjItem031]
  Rotation = 0
  ScaleType = 0
  TheoreticalExact = false
  Type = 1
  UnderTolerance = 0
  X = 13.5722
  Y = 12.1156
FEATURE [TechDraw::DrawViewDimension] Dimension159
  Arbitrary = false
  ArbitraryTolerances = false
  FormatSpec = %.2f
  FormatSpecOverTolerance = %+.2f
  FormatSpecUnderTolerance = %+.2f
  Inverted = false
  LockPosition = false
  MeasureType = 1
  OverTolerance = 0
  References2D = -> [ProjItem029]
  Rotation = 0
  ScaleType = 0
  TheoreticalExact = false
  Type = 2
  UnderTolerance = 0
  X = 37.5072
  Y = 15.9656
FEATURE [TechDraw::DrawViewDimension] Dimension160
  Arbitrary = false
  ArbitraryTolerances = false
  FormatSpec = %.2f
  FormatSpecOverTolerance = %+.2f
  FormatSpecUnderTolerance = %+.2f
  Inverted = false
  LockPosition = false
  MeasureType = 1
  OverTolerance = 0
  References2D = -> [ProjItem029]
  Rotation = 0
  ScaleType = 0
  TheoreticalExact = false
  Type = 2
  UnderTolerance = 0
  X = 56.4313
  Y = 11.1361
FEATURE [TechDraw::DrawViewDimension] Dimension161
  Arbitrary = false
  ArbitraryTolerances = false
  FormatSpec = R%.2f
  FormatSpecOverTolerance = %+.2f
  FormatSpecUnderTolerance = %+.2f
  Inverted = false
  LockPosition = false
  MeasureType = 1
  OverTolerance = 0
  References2D = -> [ProjItem031]
  Rotation = 0
  ScaleType = 0
  TheoreticalExact = false
  Type = 4
  UnderTolerance = 0
  X = 32.4588
  Y = -32.0479
FEATURE [TechDraw::DrawViewDimension] Dimension162
  Arbitrary = false
  ArbitraryTolerances = false
  FormatSpec = ⌀%.2f
  FormatSpecOverTolerance = %+.2f
  FormatSpecUnderTolerance = %+.2f
  Inverted = false
  LockPosition = false
  MeasureType = 1
  OverTolerance = 0
  References2D = -> [ProjItem031]
  Rotation = 0
  ScaleType = 0
  TheoreticalExact = false
  Type = 5
  UnderTolerance = 0
  X = 32.272
  Y = -21.9629
FEATURE [TechDraw::DrawViewDimension] Dimension163
  Arbitrary = false
  ArbitraryTolerances = false
  FormatSpec = ⌀%.2f
  FormatSpecOverTolerance = %+.2f
  FormatSpecUnderTolerance = %+.2f
  Inverted = false
  LockPosition = false
  MeasureType = 1
  OverTolerance = 0
  References2D = -> [ProjItem031]
  Rotation = 0
  ScaleType = 0
  TheoreticalExact = false
  Type = 5
  UnderTolerance = 0
  X = 29.8068
  Y = -11.8779
FEATURE [TechDraw::DrawViewDimension] Dimension164
  Arbitrary = false
  ArbitraryTolerances = false
  FormatSpec = ⌀%.2f
  FormatSpecOverTolerance = %+.2f
  FormatSpecUnderTolerance = %+.2f
  Inverted = false
  LockPosition = false
  MeasureType = 1
  OverTolerance = 0
  References2D = -> [ProjItem029]
  Rotation = 0
  ScaleType = 0
  TheoreticalExact = false
  Type = 5
  UnderTolerance = 0
  X = 41.0827
  Y = -11.6026
FEATURE [TechDraw::DrawViewDimension] Dimension165
  Arbitrary = false
  ArbitraryTolerances = false
  FormatSpec = M%.0fx0.8
  FormatSpecOverTolerance = %+.2f
  FormatSpecUnderTolerance = %+.2f
  Inverted = false
  LockPosition = false
  MeasureType = 1
  OverTolerance = 0
  References2D = -> [ProjItem031]
  Rotation = 0
  ScaleType = 0
  TheoreticalExact = false
  Type = 5
  UnderTolerance = 0
  X = 25.7777
  Y = 38.4619
FEATURE [TechDraw::DrawViewDimension] Dimension166
  Arbitrary = false
  ArbitraryTolerances = false
  FormatSpec = M%.0fx0.5
  FormatSpecOverTolerance = %+.2f
  FormatSpecUnderTolerance = %+.2f
  Inverted = false
  LockPosition = false
  MeasureType = 1
  OverTolerance = 0
  References2D = -> [ProjItem031]
  Rotation = 0
  ScaleType = 0
  TheoreticalExact = false
  Type = 5
  UnderTolerance = 0
  X = 14.7301
  Y = -11.8659
FEATURE [TechDraw::DrawLeaderLine] LeaderLine009
  AutoHorizontal = true
  EndSymbol = 7
  LeaderParent = -> ProjItem031
  LockPosition = true
  Rotation = 0
  Scalable = false
  ScaleType = 0
  StartSymbol = 0
  WayPoints = (3) [(0,0,0),(-378.275,62.2952,0),(-303.302,62.2952,0)]
  X = -40.0313
  Y = -56.1373
FEATURE [TechDraw::DrawPage] Page008  label="carriage_dwg"
  KeepUpdated = false
  NextBalloonIndex = 1
  ProjectionType = 0
  Template = -> Template008
  Views = -> [View009,ProjGroup008,DimExtent005,DimExtent006,DimExtent007,Detail,Dimension122,Dimension123,Dimension124,Dimension125,Dimension126,Dimension127,Dimension128,Dimension129,Dimension130,Dimension131,Dimension132,Dimension133,Dimension134,Dimension135,Dimension137,Dimension138,Dimension139,Dimension140,Dimension141,Dimension142,Dimension143,Dimension144,Dimension145,Dimension146,Dimension147,+18 more]
